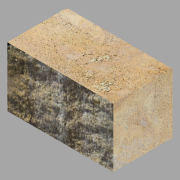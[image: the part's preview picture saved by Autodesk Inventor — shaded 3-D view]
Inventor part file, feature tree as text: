
AUTODESK INVENTOR PART (.ipt)
format: ipt  version: 2022.2 (Build 262287000, 287)  size: 150,528 bytes
history: native  units: in
note: dims shown in document units (in); Inventor stores cm internally (conversion verified against a paired STEP export)
features: extrude x1, sketch x1
ambient origin geometry x8: Origin, YZ Plane, XZ Plane, XY Plane, X Axis, Y Axis, Z Axis, Center Point
bodies: Solid1 (feature_tree)
feature tree (2):
  extrude  "Extrusion1"  Depth=18.0in
  sketch  "Sketch1"  dims[d0=18.0in d1=18.0in d2=32.0in d3=0.0in]
